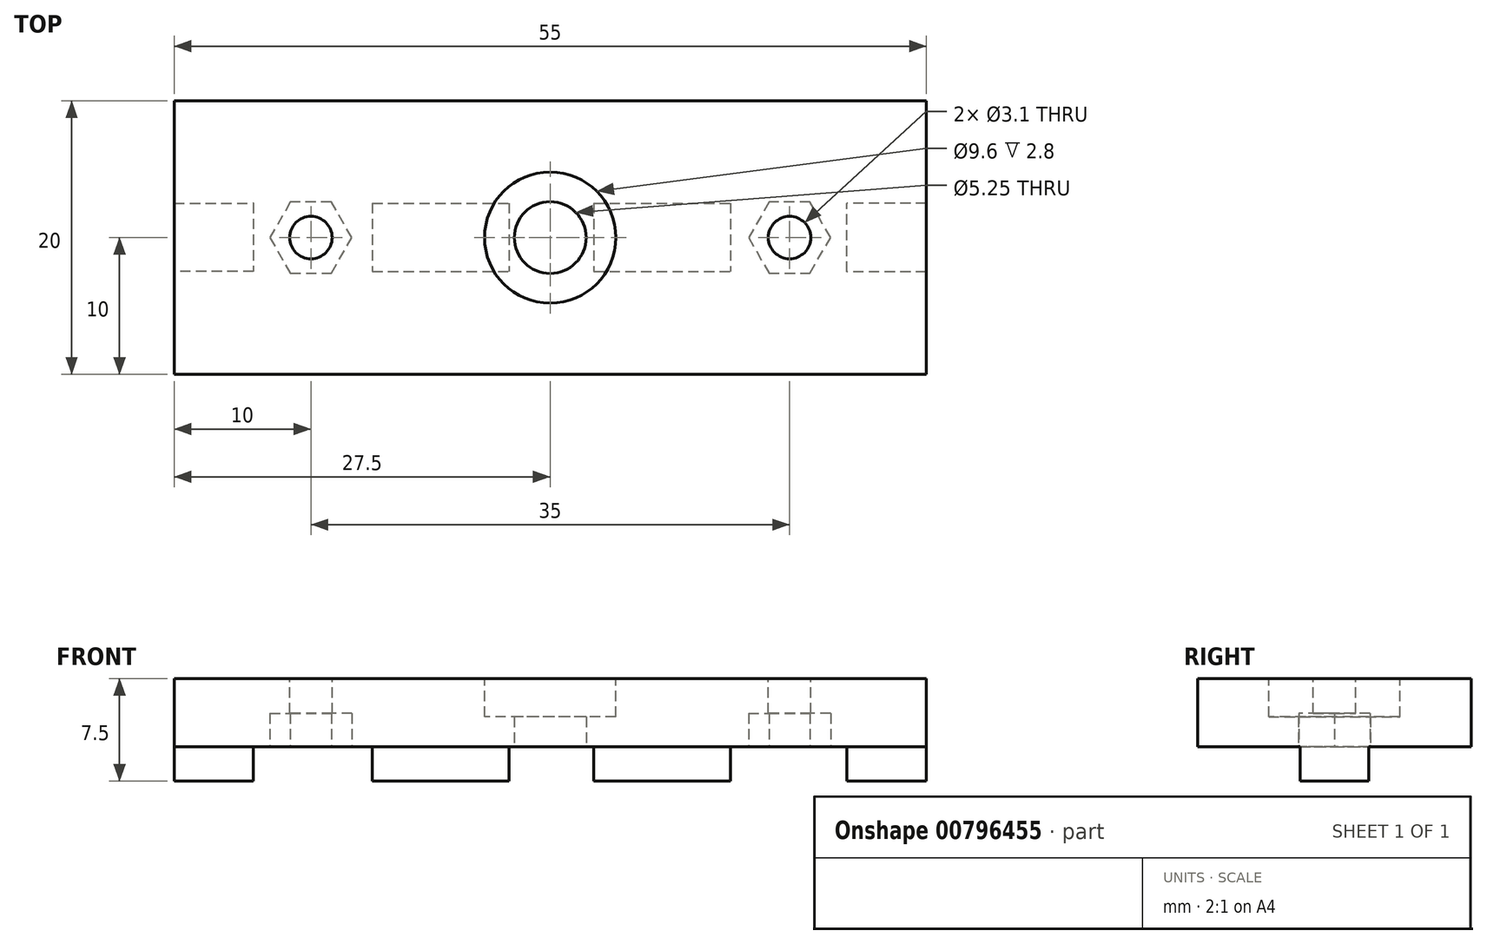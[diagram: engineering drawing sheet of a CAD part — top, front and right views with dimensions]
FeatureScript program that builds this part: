
annotation { "Feature Type Name" : "Feature", "Feature Type Description" : "" }
export const myFeature = defineFeature(function(context is Context, id is Id, definition is map)
    precondition{}
    {
        {
            var Q0;
            Q0=qCreatedBy(makeId("Top.planeOp"),FACE);
            var sketch = newSketch(context, id + "F0", { "sketchPlane" : qUnion([Q0])});
            skLineSegment(sketch, "E0.bottom", {"start": v(-27.5, 10) * mm, "end": v(27.5, 10) * mm});
            skLineSegment(sketch, "E0.top", {"start": v(-27.5, -10) * mm, "end": v(27.5, -10) * mm});
            skLineSegment(sketch, "E0.left", {"start": v(-27.5, 10) * mm, "end": v(-27.5, -10) * mm});
            skLineSegment(sketch, "E0.right", {"start": v(27.5, 10) * mm, "end": v(27.5, -10) * mm});
            skPoint(sketch, "E0.middle", {"position": v(0, 0) * mm});
            skSolve(sketch);
        }
        {
            var Q0;
            Q0=makeQuery(id+"F0.imprint","IMPRINT",FACE,{"disambiguationData":[TD([[makeQuery(id+"F0.imprint","IMPRINT",EDGE,{"derivedFrom":sQuery(id+"F0.wireOp",EDGE,"E0.bottom")}),-1.0]])]});
            extrude(context, id + "F1", {"entities" : qUnion([Q0]), "depth" : 5 * mm, "offsetDistance" : 25 * mm});
        }
        {
            var Q0;
            Q0=makeQuery(id+"F1.opExtrude","CAP_FACE",FACE,{"disambiguationData":[OSD([sQuery(id+"F0.wireOp",EDGE,"E0.bottom"),sQuery(id+"F0.wireOp",EDGE,"E0.top"),sQuery(id+"F0.wireOp",EDGE,"E0.left"),sQuery(id+"F0.wireOp",EDGE,"E0.right")])],"isStart":false});
            var sketch = newSketch(context, id + "F2", { "sketchPlane" : qUnion([Q0])});
            skCircle(sketch, "E1", {"center": v(0, 0) * mm, "radius": 4.8 * mm});
            skLineSegment(sketch, "E2", {"start": v(-27.5, -10) * mm, "end": v(-17.5, -10) * mm, "construction": true});
            skLineSegment(sketch, "E3", {"start": v(-17.5, -10) * mm, "end": v(-17.5, 10) * mm, "construction": true});
            skCircle(sketch, "E4", {"center": v(-17.5, 0) * mm, "radius": 1.55 * mm});
            skLineSegment(sketch, "E5", {"start": v(27.5, 10) * mm, "end": v(17.5, 10) * mm, "construction": true});
            skLineSegment(sketch, "E6", {"start": v(17.5, 10) * mm, "end": v(17.5, -10) * mm, "construction": true});
            skCircle(sketch, "E7", {"center": v(17.5, 0) * mm, "radius": 1.55 * mm});
            skSolve(sketch);
        }
        {
            var Q0;
            Q0=makeQuery(id+"F2.imprint","IMPRINT",FACE,{"disambiguationData":[TD([[makeQuery(id+"F2.imprint","IMPRINT",EDGE,{"derivedFrom":sQuery(id+"F2.wireOp",EDGE,"E1")}),1.0]])]});
            extrude(context, id + "F3", {"entities" : qUnion([Q0]), "operationType" : NewBodyOperationType.REMOVE, "oppositeDirection" : true, "depth" : 2.8 * mm, "offsetDistance" : 25 * mm});
        }
        {
            var Q0;
            Q0=makeQuery(id+"F1.opExtrude","CAP_FACE",FACE,{"disambiguationData":[OSD([sQuery(id+"F0.wireOp",EDGE,"E0.bottom"),sQuery(id+"F0.wireOp",EDGE,"E0.top"),sQuery(id+"F0.wireOp",EDGE,"E0.left"),sQuery(id+"F0.wireOp",EDGE,"E0.right")])],"isStart":true});
            var sketch = newSketch(context, id + "F4", { "sketchPlane" : qUnion([Q0])});
            skCircle(sketch, "E8", {"center": v(0, 0) * mm, "radius": 2.62 * mm});
            skSolve(sketch);
        }
        {
            var Q0;
            Q0=makeQuery(id+"F4.imprint","IMPRINT",FACE,{"disambiguationData":[TD([[makeQuery(id+"F4.imprint","IMPRINT",EDGE,{"derivedFrom":sQuery(id+"F4.wireOp",EDGE,"E8")}),1.0]])]});
            extrude(context, id + "F5", {"entities" : qUnion([Q0]), "operationType" : NewBodyOperationType.REMOVE, "oppositeDirection" : true, "depth" : 25 * mm, "offsetDistance" : 25 * mm});
        }
        {
            var Q0;
            Q0=makeQuery(id+"F2.imprint","IMPRINT",FACE,{"disambiguationData":[TD([[makeQuery(id+"F2.imprint","IMPRINT",EDGE,{"derivedFrom":sQuery(id+"F2.wireOp",EDGE,"E4")}),1.0]])]});
            var Q1;
            Q1=makeQuery(id+"F2.imprint","IMPRINT",FACE,{"disambiguationData":[TD([[makeQuery(id+"F2.imprint","IMPRINT",EDGE,{"derivedFrom":sQuery(id+"F2.wireOp",EDGE,"E7")}),1.0]])]});
            extrude(context, id + "F6", {"entities" : qUnion([Q0, Q1]), "operationType" : NewBodyOperationType.REMOVE, "oppositeDirection" : true, "depth" : 25 * mm, "offsetDistance" : 25 * mm});
        }
        {
            var Q0;
            Q0=makeQuery(id+"F1.opExtrude","CAP_FACE",FACE,{"disambiguationData":[OSD([sQuery(id+"F0.wireOp",EDGE,"E0.bottom"),sQuery(id+"F0.wireOp",EDGE,"E0.top"),sQuery(id+"F0.wireOp",EDGE,"E0.left"),sQuery(id+"F0.wireOp",EDGE,"E0.right")])],"isStart":true});
            var sketch = newSketch(context, id + "F7", { "sketchPlane" : qUnion([Q0])});
            skCircle(sketch, "E9.cCircle", {"center": v(-17.5, 0) * mm, "radius": 2.6 * mm, "construction": true});
            skLineSegment(sketch, "E9.0", {"start": v(-19, 2.6) * mm, "end": v(-16, 2.6) * mm});
            skLineSegment(sketch, "E9.1", {"start": v(-16, 2.6) * mm, "end": v(-14.5, 0) * mm});
            skLineSegment(sketch, "E9.2", {"start": v(-14.5, 0) * mm, "end": v(-16, -2.6) * mm});
            skLineSegment(sketch, "E9.3", {"start": v(-16, -2.6) * mm, "end": v(-19, -2.6) * mm});
            skLineSegment(sketch, "E9.4", {"start": v(-19, -2.6) * mm, "end": v(-20.5, 0) * mm});
            skLineSegment(sketch, "E9.5", {"start": v(-20.5, 0) * mm, "end": v(-19, 2.6) * mm});
            skPoint(sketch, "E9.0.midPoint", {"position": v(-17.5, 2.6) * mm});
            skCircle(sketch, "E10.cCircle", {"center": v(17.5, 0) * mm, "radius": 2.6 * mm, "construction": true});
            skLineSegment(sketch, "E10.0", {"start": v(16, 2.6) * mm, "end": v(19, 2.6) * mm});
            skLineSegment(sketch, "E10.1", {"start": v(19, 2.6) * mm, "end": v(20.5, 0) * mm});
            skLineSegment(sketch, "E10.2", {"start": v(20.5, 0) * mm, "end": v(19, -2.6) * mm});
            skLineSegment(sketch, "E10.3", {"start": v(19, -2.6) * mm, "end": v(16, -2.6) * mm});
            skLineSegment(sketch, "E10.4", {"start": v(16, -2.6) * mm, "end": v(14.5, 0) * mm});
            skLineSegment(sketch, "E10.5", {"start": v(14.5, 0) * mm, "end": v(16, 2.6) * mm});
            skPoint(sketch, "E10.0.midPoint", {"position": v(17.5, 2.6) * mm});
            skSolve(sketch);
        }
        {
            var Q0;
            Q0=makeQuery(id+"F7.imprint","IMPRINT",FACE,{"disambiguationData":[TD([[makeQuery(id+"F7.imprint","IMPRINT",EDGE,{"derivedFrom":sQuery(id+"F7.wireOp",EDGE,"E9.0")}),-1.0]])]});
            var Q1;
            Q1=makeQuery(id+"F7.imprint","IMPRINT",FACE,{"disambiguationData":[TD([[makeQuery(id+"F7.imprint","IMPRINT",EDGE,{"derivedFrom":sQuery(id+"F7.wireOp",EDGE,"E10.0")}),-1.0]])]});
            extrude(context, id + "F8", {"entities" : qUnion([Q0, Q1]), "operationType" : NewBodyOperationType.REMOVE, "oppositeDirection" : true, "depth" : 2.45 * mm, "offsetDistance" : 25 * mm});
        }
        {
            var Q0;
            Q0=makeQuery(id+"F1.opExtrude","CAP_FACE",FACE,{"disambiguationData":[OSD([sQuery(id+"F0.wireOp",EDGE,"E0.bottom"),sQuery(id+"F0.wireOp",EDGE,"E0.top"),sQuery(id+"F0.wireOp",EDGE,"E0.left"),sQuery(id+"F0.wireOp",EDGE,"E0.right")])],"isStart":true});
            var sketch = newSketch(context, id + "F9", { "sketchPlane" : qUnion([Q0])});
            skLineSegment(sketch, "E11", {"start": v(27.5, 0) * mm, "end": v(27.5, 2.5) * mm, "construction": true});
            skLineSegment(sketch, "E12.bottom", {"start": v(27.5, 2.5) * mm, "end": v(21.7, 2.5) * mm});
            skLineSegment(sketch, "E12.top", {"start": v(27.5, -2.5) * mm, "end": v(21.7, -2.5) * mm});
            skLineSegment(sketch, "E12.left", {"start": v(27.5, 2.5) * mm, "end": v(27.5, -2.5) * mm});
            skLineSegment(sketch, "E12.right", {"start": v(21.7, 2.5) * mm, "end": v(21.7, -2.5) * mm});
            skLineSegment(sketch, "E13", {"start": v(-27.5, -2.5) * mm, "end": v(-21.7, -2.53) * mm});
            skLineSegment(sketch, "E14", {"start": v(-21.7, -2.53) * mm, "end": v(-21.7, 2.47) * mm});
            skLineSegment(sketch, "E15", {"start": v(-21.7, 2.47) * mm, "end": v(-27.5, 2.47) * mm});
            skLineSegment(sketch, "E16", {"start": v(-27.5, 2.47) * mm, "end": v(-27.5, -2.5) * mm});
            skLineSegment(sketch, "E17", {"start": v(21.7, -2.5) * mm, "end": v(-21.7, -2.53) * mm, "construction": true});
            skLineSegment(sketch, "E18.bottom", {"start": v(-13.01, -2.52) * mm, "end": v(-3.01, -2.52) * mm});
            skLineSegment(sketch, "E18.top", {"start": v(-13.01, 2.48) * mm, "end": v(-3.01, 2.48) * mm});
            skLineSegment(sketch, "E18.left", {"start": v(-13.01, -2.52) * mm, "end": v(-13.01, 2.48) * mm});
            skLineSegment(sketch, "E18.right", {"start": v(-3.01, -2.52) * mm, "end": v(-3.01, 2.48) * mm});
            skLineSegment(sketch, "E19.bottom", {"start": v(3.2, -2.51) * mm, "end": v(13.2, -2.51) * mm});
            skLineSegment(sketch, "E19.top", {"start": v(3.2, 2.49) * mm, "end": v(13.2, 2.49) * mm});
            skLineSegment(sketch, "E19.left", {"start": v(3.2, -2.51) * mm, "end": v(3.2, 2.49) * mm});
            skLineSegment(sketch, "E19.right", {"start": v(13.2, -2.51) * mm, "end": v(13.2, 2.49) * mm});
            skSolve(sketch);
        }
        {
            var Q0;
            Q0=makeQuery(id+"F9.imprint","IMPRINT",FACE,{"disambiguationData":[TD([[makeQuery(id+"F9.imprint","IMPRINT",EDGE,{"derivedFrom":sQuery(id+"F9.wireOp",EDGE,"E13")}),1.0]])]});
            var Q1;
            Q1=makeQuery(id+"F9.imprint","IMPRINT",FACE,{"disambiguationData":[TD([[makeQuery(id+"F9.imprint","IMPRINT",EDGE,{"derivedFrom":sQuery(id+"F9.wireOp",EDGE,"E18.bottom")}),1.0]])]});
            var Q2;
            Q2=makeQuery(id+"F9.imprint","IMPRINT",FACE,{"disambiguationData":[TD([[makeQuery(id+"F9.imprint","IMPRINT",EDGE,{"derivedFrom":sQuery(id+"F9.wireOp",EDGE,"E19.bottom")}),1.0]])]});
            var Q3;
            Q3=makeQuery(id+"F9.imprint","IMPRINT",FACE,{"disambiguationData":[TD([[makeQuery(id+"F9.imprint","IMPRINT",EDGE,{"derivedFrom":sQuery(id+"F9.wireOp",EDGE,"E12.bottom")}),1.0]])]});
            extrude(context, id + "F10", {"entities" : qUnion([Q0, Q1, Q2, Q3]), "operationType" : NewBodyOperationType.ADD, "depth" : 2.5 * mm, "offsetDistance" : 25 * mm});
        }
    });
